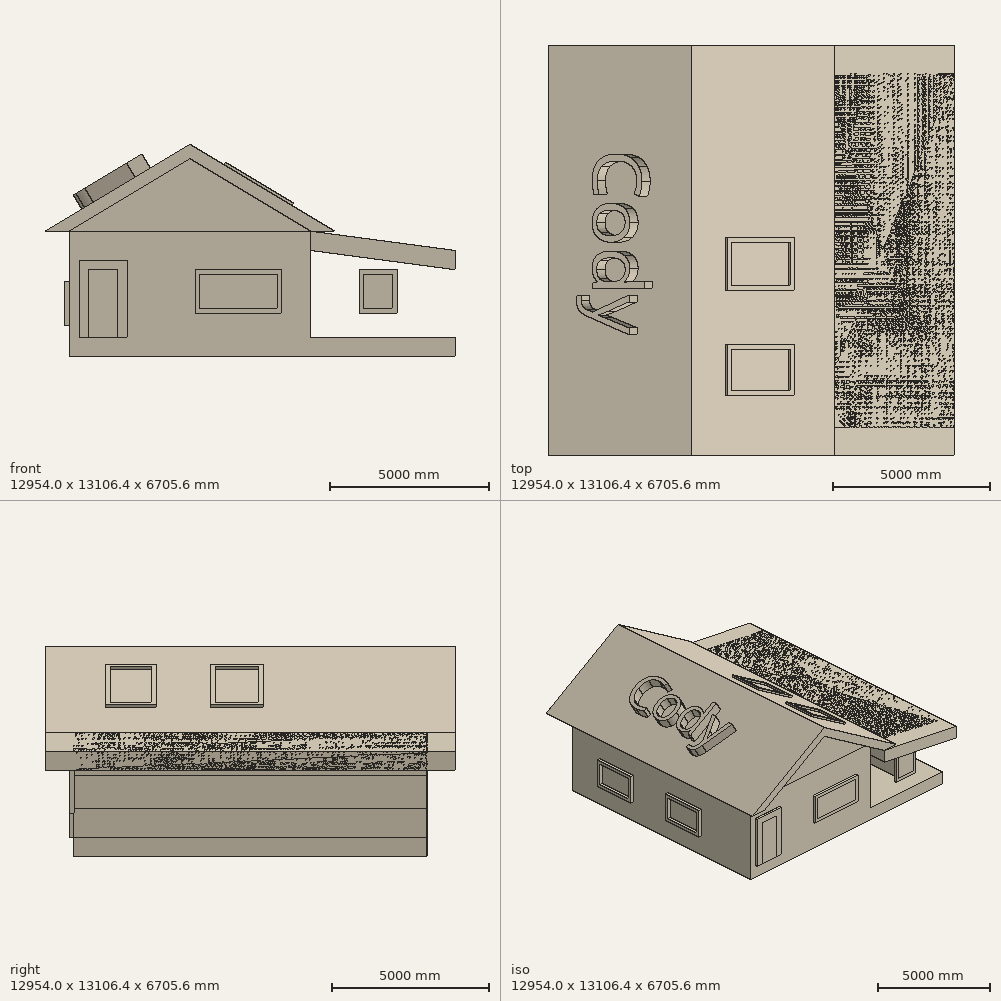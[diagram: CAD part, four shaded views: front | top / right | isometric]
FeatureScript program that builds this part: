
annotation { "Feature Type Name" : "Feature", "Feature Type Description" : "" }
export const myFeature = defineFeature(function(context is Context, id is Id, definition is map)
    precondition{}
    {
        {
            var Q0;
            Q0=qCreatedBy(makeId("Front.planeOp"),FACE);
            var sketch = newSketch(context, id + "F0", { "sketchPlane" : qUnion([Q0])});
            skLineSegment(sketch, "E0", {"start": v(0, 0) * mm, "end": v(-4572, 0) * mm});
            skLineSegment(sketch, "E1", {"start": v(0, 0) * mm, "end": v(4572, 0) * mm});
            skLineSegment(sketch, "E2", {"start": v(0, 0) * mm, "end": v(0, 2286) * mm});
            skLineSegment(sketch, "E3", {"start": v(0, 2286) * mm, "end": v(0, 2743.2) * mm});
            skLineSegment(sketch, "E4", {"start": v(0, 2743.2) * mm, "end": v(-4572, 0) * mm});
            skLineSegment(sketch, "E5", {"start": v(0, 2286) * mm, "end": v(-3810, 0) * mm});
            skLineSegment(sketch, "E6", {"start": v(0, 2743.2) * mm, "end": v(4572, 0) * mm});
            skLineSegment(sketch, "E7", {"start": v(-3810, 0) * mm, "end": v(-3810, -3352.8) * mm});
            skLineSegment(sketch, "E8", {"start": v(-3810, -3352.8) * mm, "end": v(-3810, -3962.4) * mm});
            skLineSegment(sketch, "E9", {"start": v(0, 2286) * mm, "end": v(3810, 0) * mm});
            skLineSegment(sketch, "E10", {"start": v(-3810, -3962.4) * mm, "end": v(3810, -3962.4) * mm});
            skLineSegment(sketch, "E11", {"start": v(3810, -3962.4) * mm, "end": v(8382, -3962.4) * mm});
            skLineSegment(sketch, "E12", {"start": v(3810, 0) * mm, "end": v(8381.16, -609.6) * mm});
            skLineSegment(sketch, "E13", {"start": v(8382, -3962.4) * mm, "end": v(8382, -3352.8) * mm});
            skLineSegment(sketch, "E14", {"start": v(8382, -3352.8) * mm, "end": v(8381.16, -609.6) * mm});
            skLineSegment(sketch, "E15", {"start": v(-3810, -3352.8) * mm, "end": v(-3200.4, -3352.8) * mm});
            skLineSegment(sketch, "E16", {"start": v(-3200.4, -3352.8) * mm, "end": v(-2286, -3352.8) * mm});
            skLineSegment(sketch, "E17", {"start": v(-2286, -3352.8) * mm, "end": v(8382, -3352.8) * mm});
            skLineSegment(sketch, "E18", {"start": v(-2286, -3352.8) * mm, "end": v(-2286, -1219.2) * mm});
            skLineSegment(sketch, "E19", {"start": v(-2286, -1219.2) * mm, "end": v(-3200.4, -1219.2) * mm});
            skLineSegment(sketch, "E20", {"start": v(-3200.4, -1219.2) * mm, "end": v(-3200.4, -3352.8) * mm});
            skLineSegment(sketch, "E21", {"start": v(-2286, -3352.8) * mm, "end": v(-1981.2, -3352.8) * mm});
            skLineSegment(sketch, "E22", {"start": v(-3505.2, -3352.8) * mm, "end": v(-3200.4, -3352.8) * mm});
            skLineSegment(sketch, "E23", {"start": v(-1981.2, -3352.8) * mm, "end": v(-1981.2, -914.4) * mm});
            skLineSegment(sketch, "E24", {"start": v(-3505.2, -3352.8) * mm, "end": v(-3505.2, -914.4) * mm});
            skLineSegment(sketch, "E25", {"start": v(-3505.2, -914.4) * mm, "end": v(-1981.2, -914.4) * mm});
            skPoint(sketch, "E26.startSnap0", {"position": v(-2286, -2286) * mm});
            skLineSegment(sketch, "E27", {"start": v(152.4, -1219.2) * mm, "end": v(152.4, -2590.8) * mm});
            skLineSegment(sketch, "E28", {"start": v(152.4, -1219.2) * mm, "end": v(2895.6, -1219.2) * mm});
            skLineSegment(sketch, "E29", {"start": v(2895.6, -1219.2) * mm, "end": v(2895.6, -2590.8) * mm});
            skLineSegment(sketch, "E30", {"start": v(2895.6, -2590.8) * mm, "end": v(152.4, -2590.8) * mm});
            skLineSegment(sketch, "E31", {"start": v(2743.2, -1371.6) * mm, "end": v(2743.2, -2438.4) * mm});
            skLineSegment(sketch, "E32", {"start": v(2743.2, -2438.4) * mm, "end": v(304.8, -2438.4) * mm});
            skLineSegment(sketch, "E33", {"start": v(304.8, -2438.4) * mm, "end": v(304.8, -1371.6) * mm});
            skLineSegment(sketch, "E34", {"start": v(304.8, -1371.6) * mm, "end": v(2743.2, -1371.6) * mm});
            skLineSegment(sketch, "E35", {"start": v(3810, 0) * mm, "end": v(3810, -3352.8) * mm});
            skLineSegment(sketch, "E36", {"start": v(3810, 0) * mm, "end": v(3810, -609.6) * mm});
            skLineSegment(sketch, "E37", {"start": v(8381.16, -609.6) * mm, "end": v(8381.34, -1219.2) * mm});
            skLineSegment(sketch, "E38", {"start": v(3810, -609.6) * mm, "end": v(8381.34, -1219.2) * mm});
            skLineSegment(sketch, "E39.bottom", {"start": v(5334, -2590.8) * mm, "end": v(6553.2, -2590.8) * mm});
            skLineSegment(sketch, "E39.top", {"start": v(5334, -1219.2) * mm, "end": v(6553.2, -1219.2) * mm});
            skLineSegment(sketch, "E39.left", {"start": v(5334, -2590.8) * mm, "end": v(5334, -1219.2) * mm});
            skLineSegment(sketch, "E39.right", {"start": v(6553.2, -2590.8) * mm, "end": v(6553.2, -1219.2) * mm});
            skLineSegment(sketch, "E40.bottom", {"start": v(5486.4, -1371.6) * mm, "end": v(6400.8, -1371.6) * mm});
            skLineSegment(sketch, "E40.top", {"start": v(5486.4, -2438.4) * mm, "end": v(6400.8, -2438.4) * mm});
            skLineSegment(sketch, "E40.left", {"start": v(5486.4, -1371.6) * mm, "end": v(5486.4, -2438.4) * mm});
            skLineSegment(sketch, "E40.right", {"start": v(6400.8, -1371.6) * mm, "end": v(6400.8, -2438.4) * mm});
            skText(sketch, "E41", { "text": "cody rice", "fontName": "OpenSans-Bold.ttf"});
            const initialGuessF0  = {"E41": [-9.85475, 3.90038, 1, 0, 3.02647]};
            skSetInitialGuess(sketch, initialGuessF0);
            skSolve(sketch);
        }
        {
            var Q0;
            Q0=makeQuery(id+"F0.imprint","IMPRINT",FACE,{"disambiguationData":[TD([[makeQuery(id+"F0.imprint","IMPRINT",EDGE,{"derivedFrom":sQuery(id+"F0.wireOp",EDGE,"E12")}),-1.0]])]});
            var Q1;
            Q1=makeQuery(id+"F0.imprint","IMPRINT",FACE,{"disambiguationData":[TD([[makeQuery(id+"F0.imprint","IMPRINT",EDGE,{"derivedFrom":sQuery(id+"F0.wireOp",EDGE,"E3")}),-1.0]])]});
            var Q2;
            Q2=makeQuery(id+"F0.imprint","IMPRINT",FACE,{"disambiguationData":[TD([[makeQuery(id+"F0.imprint","IMPRINT",EDGE,{"derivedFrom":sQuery(id+"F0.wireOp",EDGE,"E3")}),1.0]])]});
            extrude(context, id + "F1", {"entities" : qUnion([Q0, Q1, Q2]), "depth" : 914.4 * mm, "offsetDistance" : 30.48 * mm, "hasSecondDirection" : true, "secondDirectionOppositeDirection" : true, "secondDirectionDepth" : 12192 * mm});
        }
        {
            var Q0;
            {var subQ0=sQuery(id+"F0.wireOp",EDGE,"E2");Q0=makeQuery(id+"F0.imprint","IMPRINT",FACE,{"disambiguationData":[TD([[makeQuery(id+"F0.imprint","IMPRINT",EDGE,{"derivedFrom":subQ0}),1.0]])]});}
            var Q1;
            {var subQ0=sQuery(id+"F0.wireOp",EDGE,"E2");Q1=makeQuery(id+"F0.imprint","IMPRINT",FACE,{"disambiguationData":[TD([[makeQuery(id+"F0.imprint","IMPRINT",EDGE,{"derivedFrom":subQ0}),-1.0]])]});}
            extrude(context, id + "F2", {"entities" : qUnion([Q0, Q1]), "operationType" : NewBodyOperationType.ADD, "depth" : 30.48 * mm, "offsetDistance" : 30.48 * mm, "hasSecondDirection" : true, "secondDirectionOppositeDirection" : true, "secondDirectionDepth" : 11277.6 * mm});
        }
        {
            var Q0;
            {var subQ7=sQuery(id+"F0.wireOp",EDGE,"E7");Q0=makeQuery(id+"F0.imprint","IMPRINT",FACE,{"disambiguationData":[TD([[makeQuery(id+"F0.imprint","IMPRINT",EDGE,{"derivedFrom":subQ7}),1.0]])]});}
            var Q1;
            {var subQ0=sQuery(id+"F0.wireOp",EDGE,"E14");Q1=makeQuery(id+"F0.imprint","IMPRINT",FACE,{"disambiguationData":[TD([[makeQuery(id+"F0.imprint","IMPRINT",EDGE,{"derivedFrom":subQ0}),1.0]])]});}
            extrude(context, id + "F3", {"entities" : qUnion([Q0, Q1]), "depth" : 30.48 * mm, "offsetDistance" : 30.48 * mm, "hasSecondDirection" : true, "secondDirectionOppositeDirection" : true, "secondDirectionDepth" : 11277.6 * mm});
        }
        {
            var Q0;
            Q0=makeQuery(id+"F0.imprint","IMPRINT",FACE,{"disambiguationData":[TD([[makeQuery(id+"F0.imprint","IMPRINT",EDGE,{"derivedFrom":sQuery(id+"F0.wireOp",EDGE,"E8")}),1.0]])]});
            extrude(context, id + "F4", {"entities" : qUnion([Q0]), "operationType" : NewBodyOperationType.ADD, "depth" : 30.48 * mm, "offsetDistance" : 30.48 * mm, "hasSecondDirection" : true, "secondDirectionOppositeDirection" : true, "secondDirectionDepth" : 11277.6 * mm});
        }
        {
            var Q0;
            Q0=makeQuery(id+"F0.imprint","IMPRINT",FACE,{"disambiguationData":[TD([[makeQuery(id+"F0.imprint","IMPRINT",EDGE,{"derivedFrom":sQuery(id+"F0.wireOp",EDGE,"E31")}),-1.0]])]});
            var Q1;
            Q1=makeQuery(id+"F0.imprint","IMPRINT",FACE,{"disambiguationData":[TD([[makeQuery(id+"F0.imprint","IMPRINT",EDGE,{"derivedFrom":sQuery(id+"F0.wireOp",EDGE,"E16")}),1.0]])]});
            var Q2;
            Q2=makeQuery(id+"F0.imprint","IMPRINT",FACE,{"disambiguationData":[TD([[makeQuery(id+"F0.imprint","IMPRINT",EDGE,{"derivedFrom":sQuery(id+"F0.wireOp",EDGE,"8zFZxeUZ-u5lO-X0i2-U7lA-e2RdxMNOmcry")}),-1.0]])]});
            var Q3;
            Q3=makeQuery(id+"F0.imprint","IMPRINT",FACE,{"disambiguationData":[TD([[makeQuery(id+"F0.imprint","IMPRINT",EDGE,{"derivedFrom":sQuery(id+"F0.wireOp",EDGE,"E40.bottom")}),-1.0]])]});
            extrude(context, id + "F5", {"entities" : qUnion([Q0, Q1, Q2, Q3]), "operationType" : NewBodyOperationType.ADD, "depth" : 152.4 * mm, "offsetDistance" : 30.48 * mm, "hasSecondDirection" : true, "secondDirectionOppositeDirection" : true, "secondDirectionDepth" : 11277.6 * mm});
        }
        {
            var Q0;
            Q0=makeQuery(id+"F0.imprint","IMPRINT",FACE,{"disambiguationData":[TD([[makeQuery(id+"F0.imprint","IMPRINT",EDGE,{"derivedFrom":sQuery(id+"F0.wireOp",EDGE,"E39.bottom")}),1.0]])]});
            var Q1;
            Q1=makeQuery(id+"F0.imprint","IMPRINT",FACE,{"disambiguationData":[TD([[makeQuery(id+"F0.imprint","IMPRINT",EDGE,{"derivedFrom":sQuery(id+"F0.wireOp",EDGE,"E18")}),-1.0]])]});
            var Q2;
            Q2=makeQuery(id+"F0.imprint","IMPRINT",FACE,{"disambiguationData":[TD([[makeQuery(id+"F0.imprint","IMPRINT",EDGE,{"derivedFrom":sQuery(id+"F0.wireOp",EDGE,"E27")}),1.0]])]});
            extrude(context, id + "F6", {"entities" : qUnion([Q0, Q1, Q2]), "depth" : 152.4 * mm, "offsetDistance" : 30.48 * mm});
        }
        {
            var Q0;
            Q0=makeQuery(id+"F4.boolean.opBoolean","MERGE",FACE,{"derivedFrom":[makeQuery(id+"F3.opExtrude","SWEPT_FACE",FACE,{"disambiguationData":[OSD([sQuery(id+"F0.wireOp",EDGE,"E7")])]}),makeQuery(id+"F4.opExtrude","SWEPT_FACE",FACE,{"disambiguationData":[OSD([sQuery(id+"F0.wireOp",EDGE,"E8")])]})]});
            var sketch = newSketch(context, id + "F7", { "sketchPlane" : qUnion([Q0])});
            skLineSegment(sketch, "E42", {"start": v(-9564.8, -1603.4) * mm, "end": v(-9564.8, -2975) * mm});
            skLineSegment(sketch, "E43", {"start": v(-9564.8, -2975) * mm, "end": v(-7431.2, -2975) * mm});
            skLineSegment(sketch, "E44", {"start": v(-7431.2, -2975) * mm, "end": v(-7431.2, -1603.4) * mm});
            skLineSegment(sketch, "E45", {"start": v(-7431.2, -1603.4) * mm, "end": v(-9564.8, -1603.4) * mm});
            skLineSegment(sketch, "E46", {"start": v(-7583.6, -1755.8) * mm, "end": v(-7583.6, -2822.6) * mm});
            skLineSegment(sketch, "E47", {"start": v(-7583.6, -2822.6) * mm, "end": v(-9412.4, -2822.6) * mm});
            skLineSegment(sketch, "E48", {"start": v(-9412.4, -1755.8) * mm, "end": v(-9412.4, -2822.6) * mm});
            skLineSegment(sketch, "E49", {"start": v(-9412.4, -1755.8) * mm, "end": v(-7583.6, -1755.8) * mm});
            skLineSegment(sketch, "E50.bottom", {"start": v(-5254.79, -1603.4) * mm, "end": v(-3121.19, -1603.4) * mm});
            skLineSegment(sketch, "E50.top", {"start": v(-5254.79, -2975) * mm, "end": v(-3121.19, -2975) * mm});
            skLineSegment(sketch, "E50.left", {"start": v(-5254.79, -1603.4) * mm, "end": v(-5254.79, -2975) * mm});
            skLineSegment(sketch, "E50.right", {"start": v(-3121.19, -1603.4) * mm, "end": v(-3121.19, -2975) * mm});
            skLineSegment(sketch, "E51.bottom", {"start": v(-5102.39, -1755.8) * mm, "end": v(-3273.59, -1755.8) * mm});
            skLineSegment(sketch, "E51.top", {"start": v(-5102.39, -2822.6) * mm, "end": v(-3273.59, -2822.6) * mm});
            skLineSegment(sketch, "E51.left", {"start": v(-5102.39, -1755.8) * mm, "end": v(-5102.39, -2822.6) * mm});
            skLineSegment(sketch, "E51.right", {"start": v(-3273.59, -1755.8) * mm, "end": v(-3273.59, -2822.6) * mm});
            skSolve(sketch);
        }
        {
            var Q0;
            Q0=makeQuery(id+"F7.imprint","IMPRINT",FACE,{"disambiguationData":[TD([[makeQuery(id+"F7.imprint","IMPRINT",EDGE,{"derivedFrom":sQuery(id+"F7.wireOp",EDGE,"E42")}),1.0]])]});
            var Q1;
            Q1=makeQuery(id+"F7.imprint","IMPRINT",FACE,{"disambiguationData":[TD([[makeQuery(id+"F7.imprint","IMPRINT",EDGE,{"derivedFrom":sQuery(id+"F7.wireOp",EDGE,"E50.bottom")}),-1.0]])]});
            extrude(context, id + "F8", {"entities" : qUnion([Q0, Q1]), "operationType" : NewBodyOperationType.ADD, "depth" : 152.4 * mm, "offsetDistance" : 30.48 * mm});
        }
        {
            var Q0;
            Q0=makeQuery(id+"F1.opExtrude","SWEPT_FACE",FACE,{"disambiguationData":[OSD([sQuery(id+"F0.wireOp",EDGE,"E6")])]});
            var sketch = newSketch(context, id + "F9", { "sketchPlane" : qUnion([Q0])});
            skLineSegment(sketch, "E52.bottom", {"start": v(-152.4, 2641.13) * mm, "end": v(2351.3, 2641.13) * mm});
            skLineSegment(sketch, "E52.top", {"start": v(-152.4, 997.95) * mm, "end": v(2351.3, 997.95) * mm});
            skLineSegment(sketch, "E52.left", {"start": v(-152.4, 2641.13) * mm, "end": v(-152.4, 997.95) * mm});
            skLineSegment(sketch, "E52.right", {"start": v(2351.3, 2641.13) * mm, "end": v(2351.3, 997.95) * mm});
            skLineSegment(sketch, "E53.bottom", {"start": v(0, 2488.73) * mm, "end": v(2198.9, 2488.73) * mm});
            skLineSegment(sketch, "E53.top", {"start": v(0, 1150.35) * mm, "end": v(2198.9, 1150.35) * mm});
            skLineSegment(sketch, "E53.left", {"start": v(0, 2488.73) * mm, "end": v(0, 1150.35) * mm});
            skLineSegment(sketch, "E53.right", {"start": v(2198.9, 2488.73) * mm, "end": v(2198.9, 1150.35) * mm});
            skLineSegment(sketch, "E54.bottom", {"start": v(-152.4, 6055.5) * mm, "end": v(2351.3, 6055.5) * mm});
            skLineSegment(sketch, "E54.top", {"start": v(-152.4, 4371.88) * mm, "end": v(2351.3, 4371.88) * mm});
            skLineSegment(sketch, "E54.left", {"start": v(-152.4, 6055.5) * mm, "end": v(-152.4, 4371.88) * mm});
            skLineSegment(sketch, "E54.right", {"start": v(2351.3, 6055.5) * mm, "end": v(2351.3, 4371.88) * mm});
            skLineSegment(sketch, "E55.bottom", {"start": v(0, 5903.1) * mm, "end": v(2198.9, 5903.1) * mm});
            skLineSegment(sketch, "E55.top", {"start": v(0, 4524.28) * mm, "end": v(2198.9, 4524.28) * mm});
            skLineSegment(sketch, "E55.left", {"start": v(0, 5903.1) * mm, "end": v(0, 4524.28) * mm});
            skLineSegment(sketch, "E55.right", {"start": v(2198.9, 5903.1) * mm, "end": v(2198.9, 4524.28) * mm});
            skSolve(sketch);
        }
        {
            var Q0;
            Q0=makeQuery(id+"F9.imprint","IMPRINT",FACE,{"disambiguationData":[TD([[makeQuery(id+"F9.imprint","IMPRINT",EDGE,{"derivedFrom":sQuery(id+"F9.wireOp",EDGE,"E52.bottom")}),-1.0]])]});
            var Q1;
            Q1=makeQuery(id+"F9.imprint","IMPRINT",FACE,{"disambiguationData":[TD([[makeQuery(id+"F9.imprint","IMPRINT",EDGE,{"derivedFrom":sQuery(id+"F9.wireOp",EDGE,"E54.bottom")}),-1.0]])]});
            extrude(context, id + "F10", {"entities" : qUnion([Q0, Q1]), "operationType" : NewBodyOperationType.ADD, "depth" : 91.44 * mm, "offsetDistance" : 30.48 * mm});
        }
        {
            var Q0;
            {var subQ0=sQuery(id+"F0.wireOp",EDGE,"E16");var subQ1=sQuery(id+"F0.wireOp",EDGE,"E17");var subQ2=sQuery(id+"F0.wireOp",EDGE,"E15");Q0=makeQuery(id+"F5.boolean.opBoolean","MERGE",FACE,{"derivedFrom":[makeQuery(id+"F4.boolean.opBoolean","MERGE",FACE,{"derivedFrom":[makeQuery(id+"F3.opExtrude","CAP_FACE",FACE,{"disambiguationData":[OSD([sQuery(id+"F0.wireOp",EDGE,"E0"),sQuery(id+"F0.wireOp",EDGE,"E1"),sQuery(id+"F0.wireOp",EDGE,"E7"),sQuery(id+"F0.wireOp",EDGE,"E14"),subQ2,subQ1,sQuery(id+"F0.wireOp",EDGE,"E23"),sQuery(id+"F0.wireOp",EDGE,"E24"),sQuery(id+"F0.wireOp",EDGE,"E25"),sQuery(id+"F0.wireOp",EDGE,"E27"),sQuery(id+"F0.wireOp",EDGE,"E28"),sQuery(id+"F0.wireOp",EDGE,"E29"),sQuery(id+"F0.wireOp",EDGE,"E30"),sQuery(id+"F0.wireOp",EDGE,"E36"),sQuery(id+"F0.wireOp",EDGE,"E38"),sQuery(id+"F0.wireOp",EDGE,"E39.bottom"),sQuery(id+"F0.wireOp",EDGE,"E39.top"),sQuery(id+"F0.wireOp",EDGE,"E39.left"),sQuery(id+"F0.wireOp",EDGE,"E39.right")])],"isStart":true}),makeQuery(id+"F4.opExtrude","CAP_FACE",FACE,{"disambiguationData":[OSD([sQuery(id+"F0.wireOp",EDGE,"E8"),sQuery(id+"F0.wireOp",EDGE,"E10"),sQuery(id+"F0.wireOp",EDGE,"E11"),sQuery(id+"F0.wireOp",EDGE,"E13"),subQ2,subQ0,subQ1,sQuery(id+"F0.wireOp",EDGE,"E21"),sQuery(id+"F0.wireOp",EDGE,"E22")])],"isStart":true})]}),makeQuery(id+"F5.opExtrude","CAP_FACE",FACE,{"disambiguationData":[OSD([subQ0,sQuery(id+"F0.wireOp",EDGE,"E18"),sQuery(id+"F0.wireOp",EDGE,"E19"),sQuery(id+"F0.wireOp",EDGE,"E20")])],"isStart":true})]});}
            var sketch = newSketch(context, id + "F11", { "sketchPlane" : qUnion([Q0])});
            skSolve(sketch);
        }
        {
            var Q0;
            {var subQ24=sQuery(id+"F0.wireOp",EDGE,"E14");Q0=makeQuery(id+"F11.imprint","IMPRINT",FACE,{"disambiguationData":[TD([[makeQuery(id+"F11.imprint","IMPRINT",EDGE,{"derivedFrom":makeQuery(id+"F3.opExtrude","CAP_EDGE",EDGE,{"disambiguationData":[OSD([subQ24])],"isStart":true})}),-1.0]])]});}
            var Q1;
            Q1=makeQuery(id+"F11.imprint","IMPRINT",FACE,{"disambiguationData":[TD([[makeQuery(id+"F11.imprint","IMPRINT",EDGE,{"derivedFrom":makeQuery(id+"F3.opExtrude","CAP_EDGE",EDGE,{"disambiguationData":[OSD([sQuery(id+"F0.wireOp",EDGE,"E27")])],"isStart":true})}),-1.0]])]});
            extrude(context, id + "F12", {"entities" : qUnion([Q0, Q1]), "depth" : 30.48 * mm, "offsetDistance" : 30.48 * mm});
        }
        {
            var Q0;
            Q0=makeQuery(id+"F1.opExtrude","SWEPT_FACE",FACE,{"disambiguationData":[OSD([sQuery(id+"F0.wireOp",EDGE,"E4")])]});
            var sketch = newSketch(context, id + "F13", { "sketchPlane" : qUnion([Q0])});
            skText(sketch, "E56", { "text": "Cody", "fontName": "OpenSans-Regular.ttf"});
            const initialGuessF13  = {"E56": [-1.96986, 8.87748, 0, -1, 1.81697]};
            skSetInitialGuess(sketch, initialGuessF13);
            skSolve(sketch);
        }
        {
            var Q0;
            Q0 = qSketchRegion(id + "F13", true);
            extrude(context, id + "F14", {"entities" : qUnion([Q0]), "operationType" : NewBodyOperationType.ADD, "depth" : 518.16 * mm, "offsetDistance" : 30.48 * mm});
        }
    });
